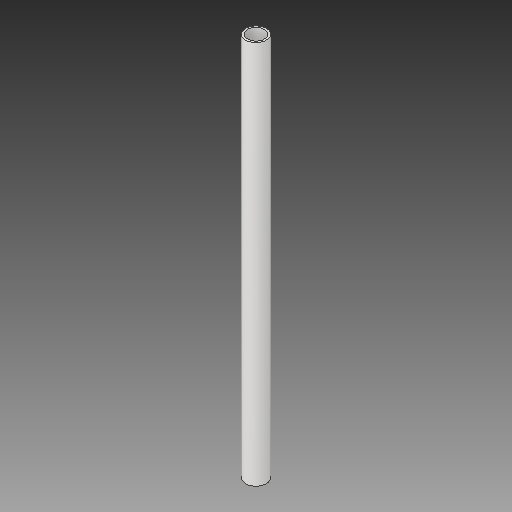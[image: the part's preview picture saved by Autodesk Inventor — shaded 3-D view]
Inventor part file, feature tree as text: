
AUTODESK INVENTOR PART (.ipt)
format: ipt  version: 2017 (Build 210142000, 142)  size: 92,672 bytes
history: native  units: in
note: dims shown in document units (in); Inventor stores cm internally (conversion verified against a paired STEP export)
features: extrude x1, sketch x1
ambient origin geometry x8: Origin, YZ Plane, XZ Plane, XY Plane, X Axis, Y Axis, Z Axis, Center Point
bodies: Solid1 (feature_tree)
feature tree (2):
  extrude  "Extrusion1"  Depth=30.0in
  sketch  "Sketch1"  dims[d0=1.625in d1=1.329in d2=30.0in d3=0.0in]
